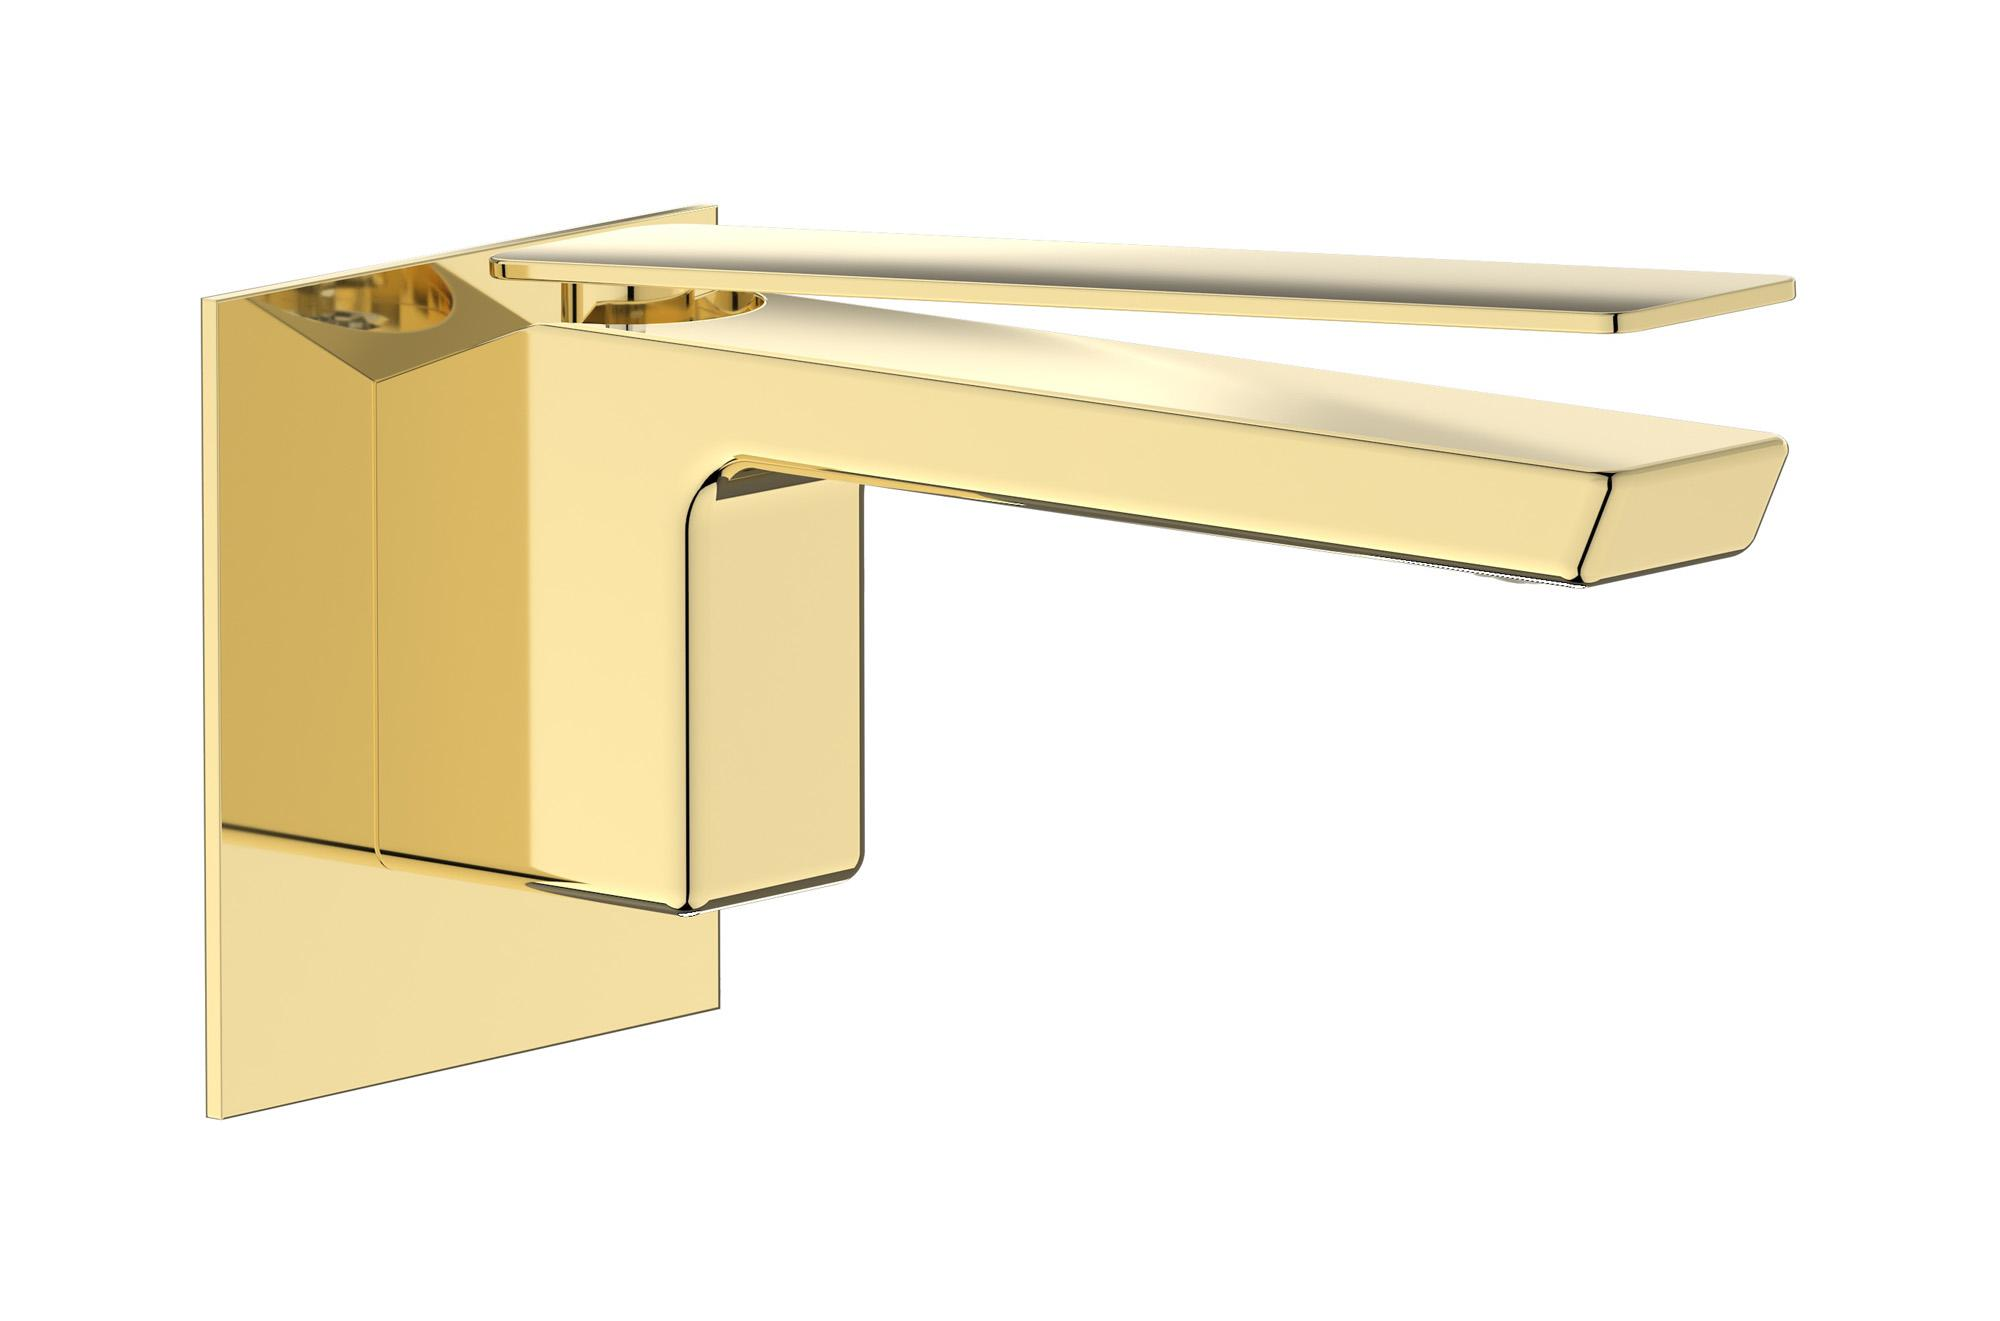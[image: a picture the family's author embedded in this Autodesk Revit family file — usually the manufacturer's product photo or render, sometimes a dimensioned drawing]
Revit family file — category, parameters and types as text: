
# Revit family: K3209
name_source: partatom
category: Apparecchi idraulici
units: mm (PartAtom-declared; Revit-internal decimal feet)

## family parameters
Basato su piano di lavoro = No
Condiviso = No
Mantieni orientamento annotazione = No
Numero OmniClass = 23.45.55.17
Punto di calcolo locali = No
Quota connettore circolare = Usa diametro
Sempre verticale = Sì
Taglio con vuoti quando caricato = No
Tipo di parte = Normale
Titolo OmniClass = Mixing Faucets

## types (8) — shared parameters
Cold water inlet = 10 mm  [stored 0.0328084 ft]
Commenti sul tipo = Washbasin mixer
Connessione CW = No
Connessione HW = No
Connessione di scarico = No
Connessione di ventilazione = No
Descrizione = Monohole wall mounted washbasin mixer
Hot water inlet = 10 mm  [stored 0.0328084 ft]
Produttore = IB Rubinetterie S.p.A.
URL = https://www.weareib.it
zero-valued in all types: Prospetto di default

## per-type parameters (varying)
| type | Finishes surface | Immagine tipo | Modello |
| Chrome | IB_Chrome | K3209CC.jpg | K3209CC |
| Brushed nickel | IB_Brushed nickel | K3209SS.jpg | K3209SS |
| Matt white | IB_matt white | K3209BO.jpg | K3209BO |
| Matt black | IB_matt black | K3209NP.jpg | K3209NP |
| Pale gold | IB_Pale gold | K3209II.jpg | K3209II |
| Brushed pale gold | IB_brushed pale gold | K3209IS.jpg | K3209IS |
| Rose gold | IB_Rose gold | K3209RS.jpg | K3209RS |
| Gold | IB_gold | K3209OO.jpg | K3209OO |

note: [stored X ft] marks values corroborated as IEEE doubles in the binary element streams (Revit-internal decimal feet)
